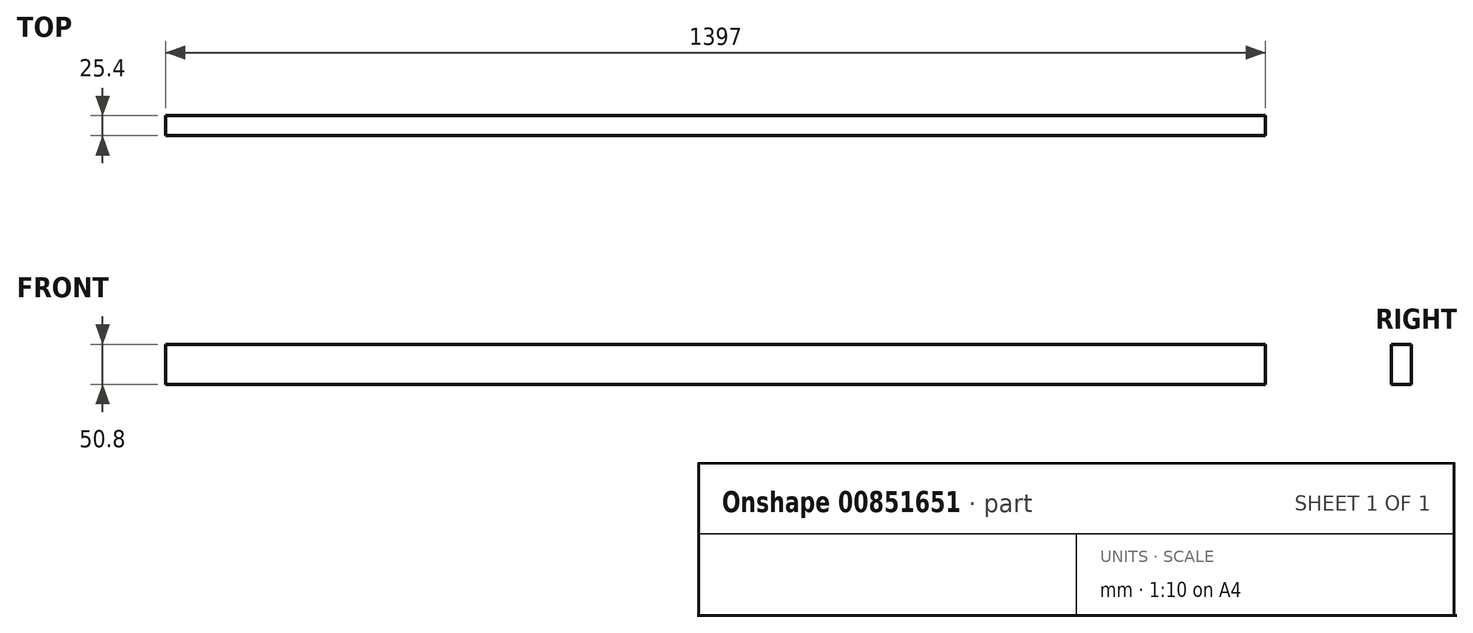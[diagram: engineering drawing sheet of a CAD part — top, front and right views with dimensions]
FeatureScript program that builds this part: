
annotation { "Feature Type Name" : "Feature", "Feature Type Description" : "" }
export const myFeature = defineFeature(function(context is Context, id is Id, definition is map)
    precondition{}
    {
        {
            var Q0;
            Q0=qCreatedBy(makeId("Top.planeOp"),FACE);
            var sketch = newSketch(context, id + "F0", { "sketchPlane" : qUnion([Q0])});
            skLineSegment(sketch, "E0", {"start": v(-718.03, -50.36) * mm, "end": v(678.97, -50.36) * mm});
            skLineSegment(sketch, "E1", {"start": v(-718.03, -50.36) * mm, "end": v(-718.03, -75.76) * mm});
            skLineSegment(sketch, "E2", {"start": v(-718.03, -75.76) * mm, "end": v(678.97, -75.76) * mm});
            skLineSegment(sketch, "E3", {"start": v(678.97, -50.36) * mm, "end": v(678.97, -75.76) * mm});
            skSolve(sketch);
        }
        {
            var Q0;
            Q0 = qSketchRegion(id + "F0", true);
            extrude(context, id + "F1", {"entities" : qUnion([Q0]), "depth" : 50.8 * mm, "offsetDistance" : 25.4 * mm});
        }
    });
